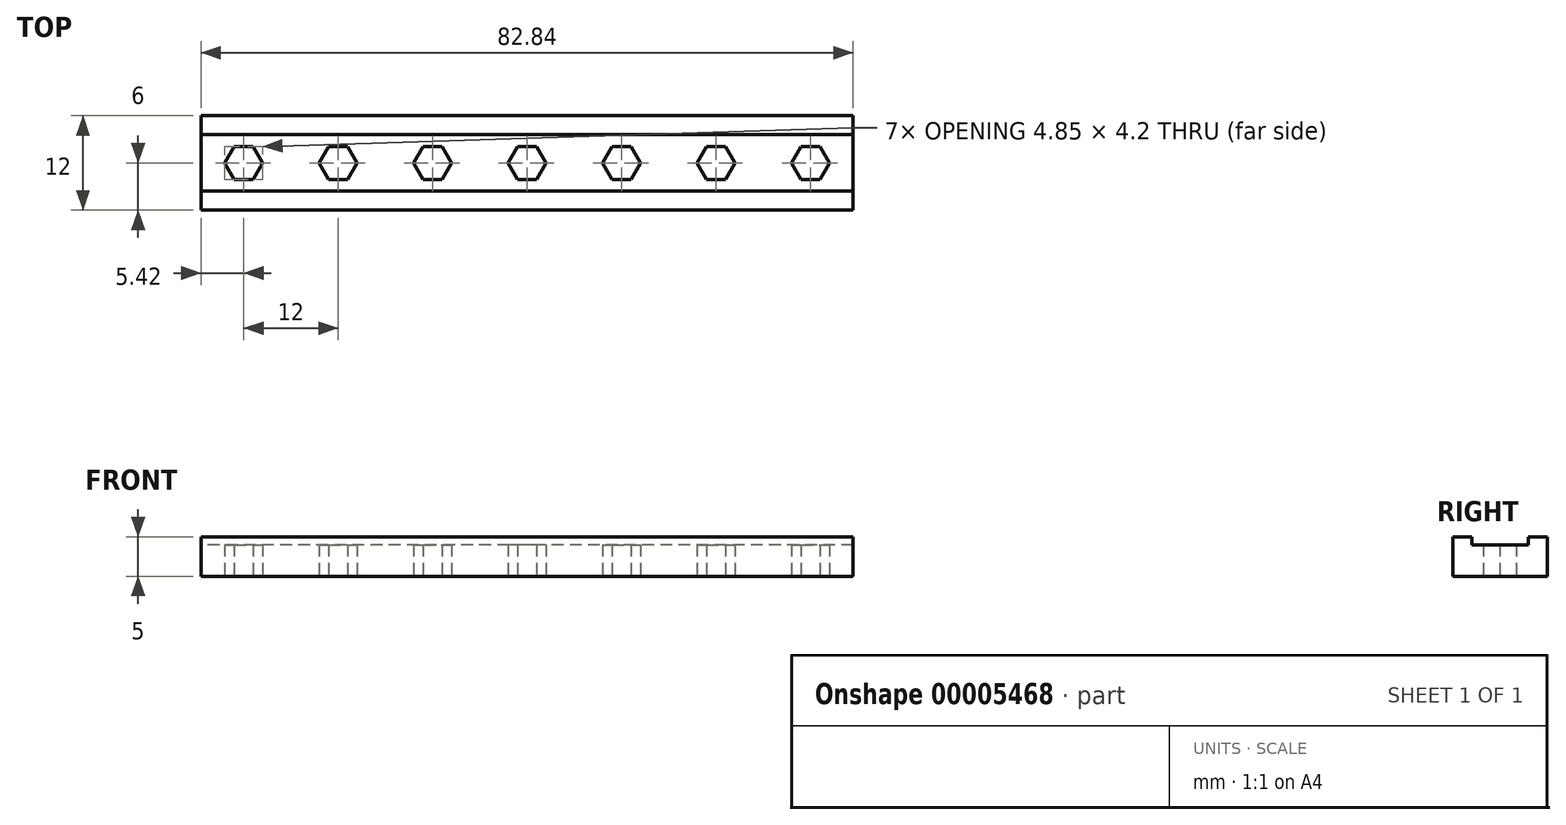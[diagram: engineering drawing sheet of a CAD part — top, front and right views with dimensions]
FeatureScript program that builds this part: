
annotation { "Feature Type Name" : "Feature", "Feature Type Description" : "" }
export const myFeature = defineFeature(function(context is Context, id is Id, definition is map)
    precondition{}
    {
        {
            var Q0;
            Q0=qCreatedBy(makeId("Top.planeOp"),FACE);
            var sketch = newSketch(context, id + "F0", { "sketchPlane" : qUnion([Q0])});
            skLineSegment(sketch, "E0.rect.bottom", {"start": v(41.42, 6) * mm, "end": v(-41.42, 6) * mm});
            skLineSegment(sketch, "E0.rect.top", {"start": v(41.42, -6) * mm, "end": v(-41.42, -6) * mm});
            skLineSegment(sketch, "E0.rect.left", {"start": v(41.42, 6) * mm, "end": v(41.42, -6) * mm});
            skLineSegment(sketch, "E0.rect.right", {"start": v(-41.42, 6) * mm, "end": v(-41.42, -6) * mm});
            skPoint(sketch, "E0.rect.middle", {"position": v(0, 0) * mm});
            skLineSegment(sketch, "E1.rect.bottom", {"start": v(41.42, 3.6) * mm, "end": v(-41.42, 3.6) * mm});
            skLineSegment(sketch, "E1.rect.top", {"start": v(41.42, -3.6) * mm, "end": v(-41.42, -3.6) * mm});
            skLineSegment(sketch, "E1.rect.left", {"start": v(41.42, 3.6) * mm, "end": v(41.42, -3.6) * mm});
            skLineSegment(sketch, "E1.rect.right", {"start": v(-41.42, 3.6) * mm, "end": v(-41.42, -3.6) * mm});
            skCircle(sketch, "E2.cCircle", {"center": v(0, 0) * mm, "radius": 2.1 * mm, "construction": true});
            skLineSegment(sketch, "E2.0", {"start": v(1.21, -2.1) * mm, "end": v(-1.21, -2.1) * mm});
            skLineSegment(sketch, "E2.1", {"start": v(-1.21, -2.1) * mm, "end": v(-2.42, 0) * mm});
            skLineSegment(sketch, "E2.2", {"start": v(-2.42, 0) * mm, "end": v(-1.21, 2.1) * mm});
            skLineSegment(sketch, "E2.3", {"start": v(-1.21, 2.1) * mm, "end": v(1.21, 2.1) * mm});
            skLineSegment(sketch, "E2.4", {"start": v(1.21, 2.1) * mm, "end": v(2.42, 0) * mm});
            skLineSegment(sketch, "E2.5", {"start": v(2.42, 0) * mm, "end": v(1.21, -2.1) * mm});
            skPoint(sketch, "E2.0.midPoint", {"position": v(0, -2.1) * mm});
            skLineSegment(sketch, "E3.1.0.0", {"start": v(10.79, 2.1) * mm, "end": v(13.21, 2.1) * mm});
            skLineSegment(sketch, "E3.1.0.1", {"start": v(13.21, 2.1) * mm, "end": v(14.42, 0) * mm});
            skLineSegment(sketch, "E3.1.0.2", {"start": v(14.42, 0) * mm, "end": v(13.21, -2.1) * mm});
            skLineSegment(sketch, "E3.1.0.3", {"start": v(13.21, -2.1) * mm, "end": v(10.79, -2.1) * mm});
            skLineSegment(sketch, "E3.1.0.4", {"start": v(10.79, -2.1) * mm, "end": v(9.58, 0) * mm});
            skLineSegment(sketch, "E3.1.0.5", {"start": v(9.58, 0) * mm, "end": v(10.79, 2.1) * mm});
            skLineSegment(sketch, "E3.2.0.0", {"start": v(22.79, 2.1) * mm, "end": v(25.21, 2.1) * mm});
            skLineSegment(sketch, "E3.2.0.1", {"start": v(25.21, 2.1) * mm, "end": v(26.42, 0) * mm});
            skLineSegment(sketch, "E3.2.0.2", {"start": v(26.42, 0) * mm, "end": v(25.21, -2.1) * mm});
            skLineSegment(sketch, "E3.2.0.3", {"start": v(25.21, -2.1) * mm, "end": v(22.79, -2.1) * mm});
            skLineSegment(sketch, "E3.2.0.4", {"start": v(22.79, -2.1) * mm, "end": v(21.58, 0) * mm});
            skLineSegment(sketch, "E3.2.0.5", {"start": v(21.58, 0) * mm, "end": v(22.79, 2.1) * mm});
            skLineSegment(sketch, "E3.direction1", {"start": v(-1.21, 2.1) * mm, "end": v(10.79, 2.1) * mm, "construction": true});
            skLineSegment(sketch, "E4.1.0.0", {"start": v(-14.42, 0) * mm, "end": v(-13.21, 2.1) * mm});
            skLineSegment(sketch, "E4.1.0.1", {"start": v(-10.79, 2.1) * mm, "end": v(-9.58, 0) * mm});
            skLineSegment(sketch, "E4.1.0.2", {"start": v(-13.21, 2.1) * mm, "end": v(-10.79, 2.1) * mm});
            skLineSegment(sketch, "E4.1.0.3", {"start": v(-9.58, 0) * mm, "end": v(-10.79, -2.1) * mm});
            skLineSegment(sketch, "E4.1.0.4", {"start": v(-10.79, -2.1) * mm, "end": v(-13.21, -2.1) * mm});
            skLineSegment(sketch, "E4.1.0.5", {"start": v(-13.21, -2.1) * mm, "end": v(-14.42, 0) * mm});
            skLineSegment(sketch, "E4.2.0.0", {"start": v(-26.42, 0) * mm, "end": v(-25.21, 2.1) * mm});
            skLineSegment(sketch, "E4.2.0.1", {"start": v(-22.79, 2.1) * mm, "end": v(-21.58, 0) * mm});
            skLineSegment(sketch, "E4.2.0.2", {"start": v(-25.21, 2.1) * mm, "end": v(-22.79, 2.1) * mm});
            skLineSegment(sketch, "E4.2.0.3", {"start": v(-21.58, 0) * mm, "end": v(-22.79, -2.1) * mm});
            skLineSegment(sketch, "E4.2.0.4", {"start": v(-22.79, -2.1) * mm, "end": v(-25.21, -2.1) * mm});
            skLineSegment(sketch, "E4.2.0.5", {"start": v(-25.21, -2.1) * mm, "end": v(-26.42, 0) * mm});
            skLineSegment(sketch, "E4.direction1", {"start": v(-2.42, 0) * mm, "end": v(-14.42, 0) * mm, "construction": true});
            skLineSegment(sketch, "E5.0.3.0", {"start": v(34.79, 2.1) * mm, "end": v(37.21, 2.1) * mm});
            skLineSegment(sketch, "E5.3.3.0", {"start": v(37.21, 2.1) * mm, "end": v(38.42, 0) * mm});
            skLineSegment(sketch, "E5.6.3.0", {"start": v(38.42, 0) * mm, "end": v(37.21, -2.1) * mm});
            skLineSegment(sketch, "E5.9.3.0", {"start": v(37.21, -2.1) * mm, "end": v(34.79, -2.1) * mm});
            skLineSegment(sketch, "E5.12.3.0", {"start": v(34.79, -2.1) * mm, "end": v(33.58, 0) * mm});
            skLineSegment(sketch, "E5.15.3.0", {"start": v(33.58, 0) * mm, "end": v(34.79, 2.1) * mm});
            skLineSegment(sketch, "E6.0.3.0", {"start": v(-38.42, 0) * mm, "end": v(-37.21, 2.1) * mm});
            skLineSegment(sketch, "E6.3.3.0", {"start": v(-34.79, 2.1) * mm, "end": v(-33.58, 0) * mm});
            skLineSegment(sketch, "E6.6.3.0", {"start": v(-37.21, 2.1) * mm, "end": v(-34.79, 2.1) * mm});
            skLineSegment(sketch, "E6.9.3.0", {"start": v(-33.58, 0) * mm, "end": v(-34.79, -2.1) * mm});
            skLineSegment(sketch, "E6.12.3.0", {"start": v(-34.79, -2.1) * mm, "end": v(-37.21, -2.1) * mm});
            skLineSegment(sketch, "E6.15.3.0", {"start": v(-37.21, -2.1) * mm, "end": v(-38.42, 0) * mm});
            skSolve(sketch);
        }
        {
            var Q0;
            Q0=makeQuery(id+"F0.imprint","IMPRINT",FACE,{"disambiguationData":[TD([[makeQuery(id+"F0.imprint","IMPRINT",EDGE,{"derivedFrom":sQuery(id+"F0.wireOp",EDGE,"E1.rect.bottom")}),1.0]])]});
            extrude(context, id + "F1", {"entities" : qUnion([Q0]), "depth" : 4 * mm});
        }
        {
            var Q0;
            {var subQ2=sQuery(id+"F0.wireOp",EDGE,"E0.rect.bottom");Q0=makeQuery(id+"F0.imprint","IMPRINT",FACE,{"disambiguationData":[TD([[makeQuery(id+"F0.imprint","IMPRINT",EDGE,{"derivedFrom":subQ2}),1.0]])]});}
            var Q1;
            {var subQ2=sQuery(id+"F0.wireOp",EDGE,"E0.rect.top");Q1=makeQuery(id+"F0.imprint","IMPRINT",FACE,{"disambiguationData":[TD([[makeQuery(id+"F0.imprint","IMPRINT",EDGE,{"derivedFrom":subQ2}),-1.0]])]});}
            extrude(context, id + "F2", {"entities" : qUnion([Q0, Q1]), "operationType" : NewBodyOperationType.ADD, "depth" : 5 * mm});
        }
    });
